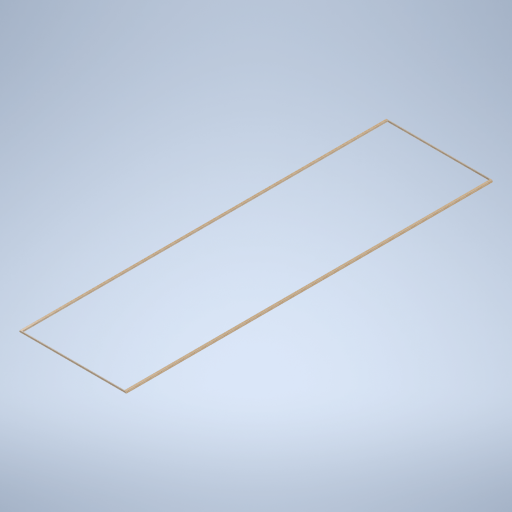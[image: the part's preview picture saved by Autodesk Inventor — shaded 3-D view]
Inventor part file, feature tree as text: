
AUTODESK INVENTOR PART (.ipt)
format: ipt  version: 2024.2 (Build 282272000, 272)  size: 274,432 bytes
history: native  units: mm
features: extrude x2, sketch x2, projected_geometry x1
ambient origin geometry x8: Origin, YZ Plane, XZ Plane, XY Plane, X Axis, Y Axis, Z Axis, Center Point
bodies: Solid1 (feature_tree)
feature tree (5):
  extrude  "Extrusion1"  Depth=9034.0mm
  extrude  "Extrusion3"  TaperAngle=0.0deg  [1 undecoded]
  sketch  "Sketch1"  dims[d1=32302.0mm d2=0.0mm d7=9034.0mm]
  sketch  "Sketch2"  dims[d8=32202.0mm d9=0.0mm d10=0.0mm]
  projected_geometry  "Projected Loop1"
note: 1 required parameter value undecoded (feature->parameter linkage not recoverable at this tier; creation-order binding heuristic only, values carry confidence <= 0.55)
